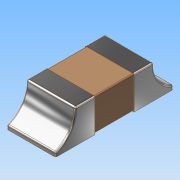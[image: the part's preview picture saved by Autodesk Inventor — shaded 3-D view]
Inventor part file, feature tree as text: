
AUTODESK INVENTOR PART (.ipt)
format: ipt  version: 2016 (Build 200138000, 138)  size: 189,440 bytes
history: native  units: mm
features: extrude x3, fillet x3, sketch x2, mirror x1, projected_geometry x1
ambient origin geometry x8: Origin, YZ Plane, XZ Plane, XY Plane, X Axis, Y Axis, Z Axis, Center Point
bodies: Body1 (feature_tree)
feature tree (10):
  extrude  "Extrusion4"  Depth=0.825mm
  sketch  "Sketch11"  dims[d9=1.225mm d10=0.0mm d11=1.25mm d12=0.5mm d13=0.0mm d14=0.1mm d15=1.0mm d16=0.0mm d17=0.75mm d18=0.0425mm d19=0.03mm]
  extrude  "Extrusion5"  Depth=1.25mm
  extrude  "Extrusion6"  Depth=0.5mm TaperAngle=0.0deg
  fillet  "Fillet1"  Radius=0.1mm
  fillet  "Fillet2"  Radius=1.0mm
  mirror  "Mirror1"
  fillet  "Fillet3"  Radius=0.75mm
  sketch  "Sketch10"  dims[d7=1.0mm d8=0.825mm]
  projected_geometry  "Projected Loop1"
